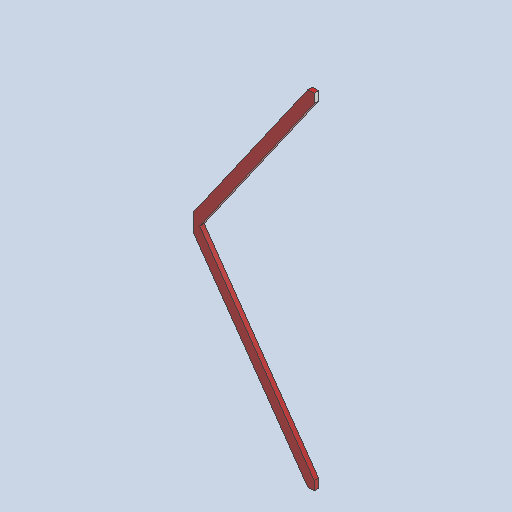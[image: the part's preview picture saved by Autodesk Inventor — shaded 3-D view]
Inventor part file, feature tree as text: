
AUTODESK INVENTOR PART (.ipt)
format: ipt  version: 2025 (Build 290162000, 162)  size: 97,280 bytes
history: native  units: in
note: dims shown in document units (in); Inventor stores cm internally (conversion verified against a paired STEP export)
features: other x4, sketch x1
ambient origin geometry x8: Origin, YZ Plane, XZ Plane, XY Plane, X Axis, Y Axis, Z Axis, Center Point
bodies: Solid1 (feature_tree)
feature tree (5):
  other  "side2.ipt"
  other  "Solid1::side2.ipt"
  other  "TaggingFeature1"
  sketch  "Sketch1"  dims[d0=0.3937in]
  other  "Finish1"
